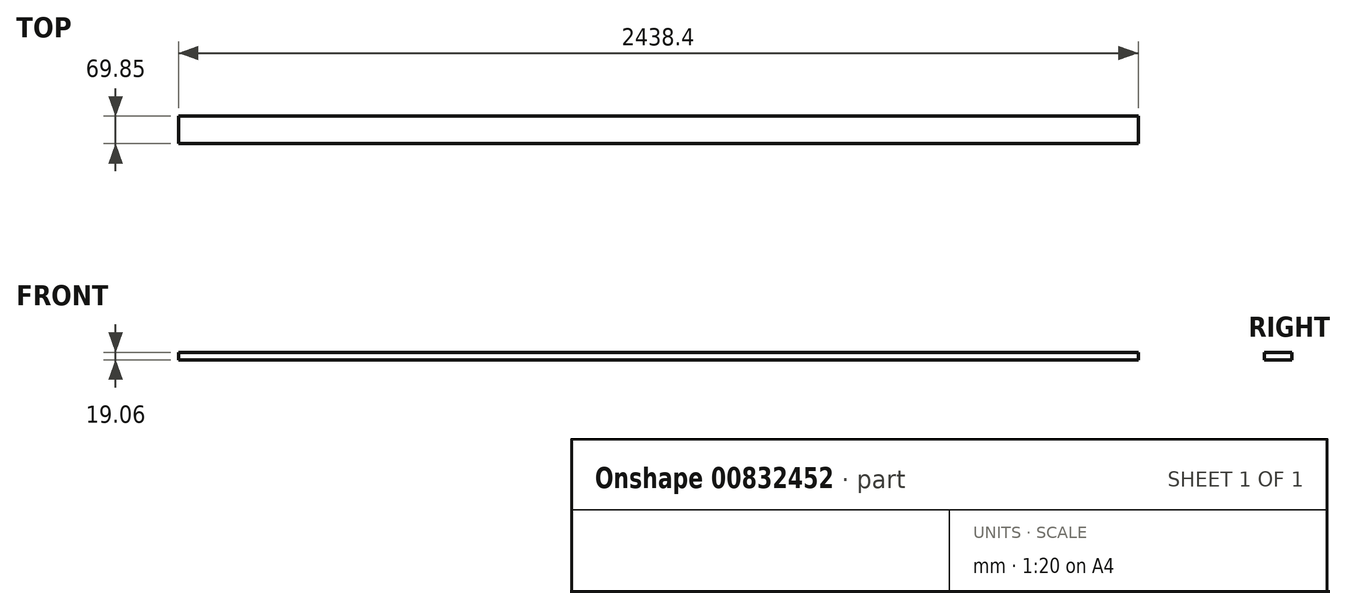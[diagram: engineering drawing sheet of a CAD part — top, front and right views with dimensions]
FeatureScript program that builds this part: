
annotation { "Feature Type Name" : "Feature", "Feature Type Description" : "" }
export const myFeature = defineFeature(function(context is Context, id is Id, definition is map)
    precondition{}
    {
        {
            var Q0;
            Q0=qCreatedBy(makeId("Front.planeOp"),FACE);
            var sketch = newSketch(context, id + "F0", { "sketchPlane" : qUnion([Q0])});
            skLineSegment(sketch, "E0.bottom", {"start": v(1219.2, -9.53) * mm, "end": v(-1219.2, -9.53) * mm});
            skLineSegment(sketch, "E0.top", {"start": v(1219.2, 9.53) * mm, "end": v(-1219.2, 9.52) * mm});
            skLineSegment(sketch, "E0.left", {"start": v(1219.2, -9.53) * mm, "end": v(1219.2, 9.53) * mm});
            skLineSegment(sketch, "E0.right", {"start": v(-1219.2, -9.53) * mm, "end": v(-1219.2, 9.52) * mm});
            skPoint(sketch, "E0.middle", {"position": v(0, 0) * mm});
            skSolve(sketch);
        }
        {
            var Q0;
            Q0 = qSketchRegion(id + "F0", true);
            extrude(context, id + "F1", {"entities" : qUnion([Q0]), "depth" : 69.85 * mm, "offsetDistance" : 25.4 * mm});
        }
    });
